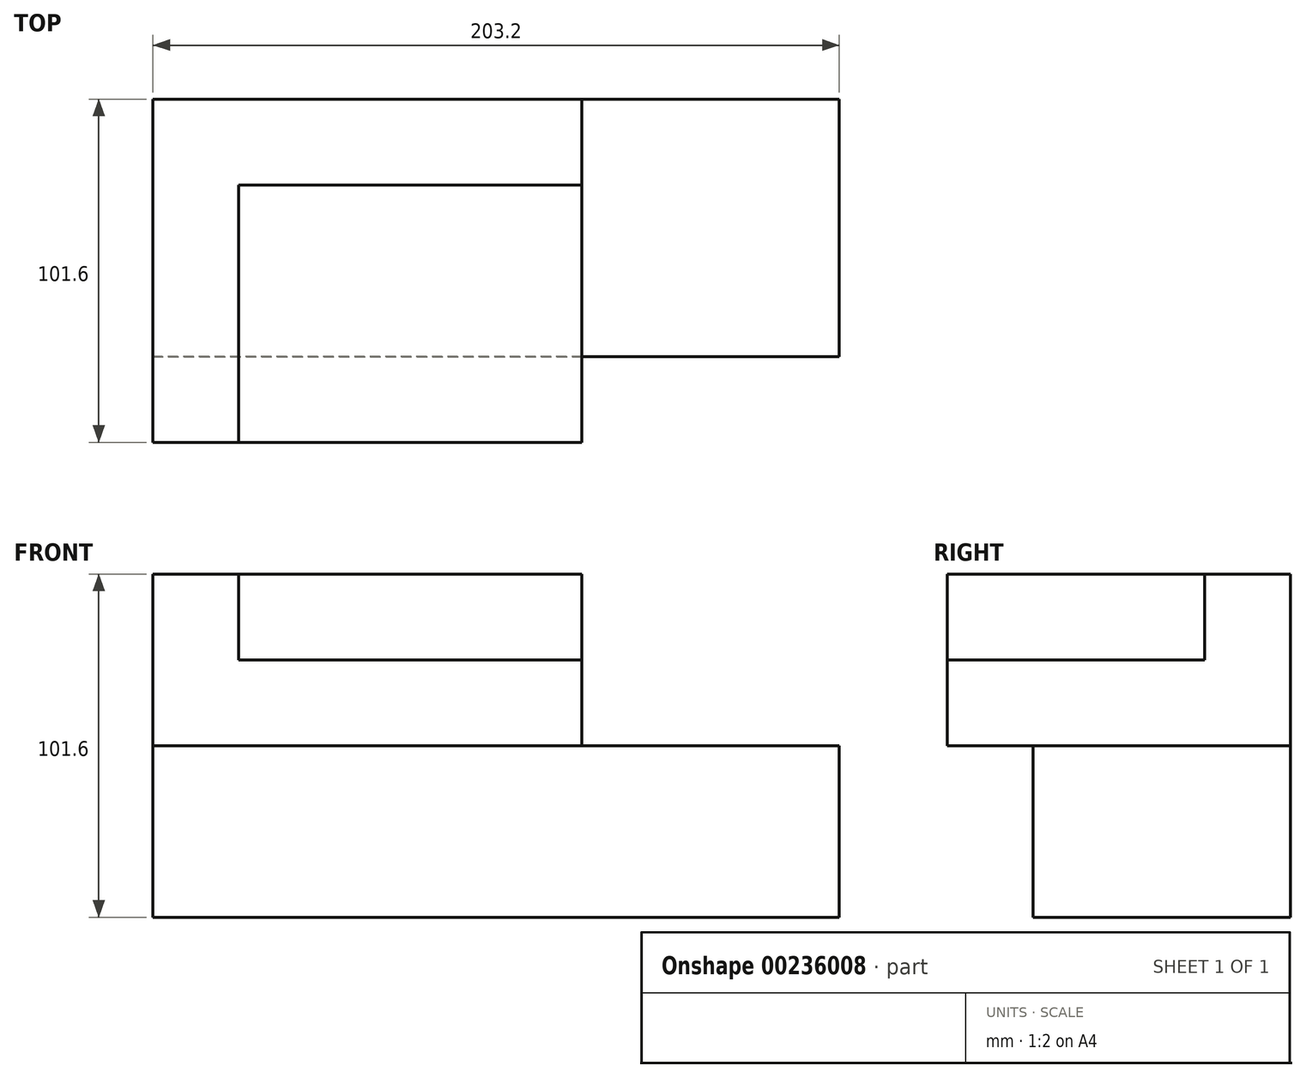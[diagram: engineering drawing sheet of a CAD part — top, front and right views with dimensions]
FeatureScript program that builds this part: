
annotation { "Feature Type Name" : "Feature", "Feature Type Description" : "" }
export const myFeature = defineFeature(function(context is Context, id is Id, definition is map)
    precondition{}
    {
        {
            var Q0;
            Q0=qCreatedBy(makeId("Top.planeOp"),FACE);
            var sketch = newSketch(context, id + "F0", { "sketchPlane" : qUnion([Q0])});
            skLineSegment(sketch, "E0.bottom", {"start": v(-172.4, -39.52) * mm, "end": v(30.8, -39.52) * mm});
            skLineSegment(sketch, "E0.top", {"start": v(-172.4, 36.68) * mm, "end": v(30.8, 36.68) * mm});
            skLineSegment(sketch, "E0.left", {"start": v(-172.4, -39.52) * mm, "end": v(-172.4, 36.68) * mm});
            skLineSegment(sketch, "E0.right", {"start": v(30.8, -39.52) * mm, "end": v(30.8, 36.68) * mm});
            skSolve(sketch);
        }
        {
            var Q0;
            Q0=makeQuery(id+"F0.imprint","IMPRINT",FACE,{"disambiguationData":[TD([[makeQuery(id+"F0.imprint","IMPRINT",EDGE,{"derivedFrom":sQuery(id+"F0.wireOp",EDGE,"E0.bottom")}),1.0]])]});
            extrude(context, id + "F1", {"entities" : qUnion([Q0]), "depth" : 50.8 * mm});
        }
        {
            var Q0;
            Q0=makeQuery(id+"F1.opExtrude","CAP_FACE",FACE,{"disambiguationData":[OSD([sQuery(id+"F0.wireOp",EDGE,"E0.bottom"),sQuery(id+"F0.wireOp",EDGE,"E0.top"),sQuery(id+"F0.wireOp",EDGE,"E0.left"),sQuery(id+"F0.wireOp",EDGE,"E0.right")])],"isStart":false});
            var sketch = newSketch(context, id + "F2", { "sketchPlane" : qUnion([Q0])});
            skLineSegment(sketch, "E1.bottom", {"start": v(-172.4, 36.68) * mm, "end": v(-45.4, 36.68) * mm});
            skLineSegment(sketch, "E1.top", {"start": v(-172.4, -64.92) * mm, "end": v(-45.4, -64.92) * mm});
            skLineSegment(sketch, "E1.left", {"start": v(-172.4, 36.68) * mm, "end": v(-172.4, -64.92) * mm});
            skLineSegment(sketch, "E1.right", {"start": v(-45.4, 36.68) * mm, "end": v(-45.4, -64.92) * mm});
            skSolve(sketch);
        }
        {
            var Q0;
            {var subQ0=sQuery(id+"F2.wireOp",EDGE,"E1.bottom");Q0=makeQuery(id+"F2.imprint","IMPRINT",FACE,{"disambiguationData":[TD([[makeQuery(id+"F2.imprint","IMPRINT",EDGE,{"derivedFrom":subQ0}),-1.0]])]});}
            extrude(context, id + "F3", {"entities" : qUnion([Q0]), "operationType" : NewBodyOperationType.ADD, "depth" : 25.4 * mm});
        }
        {
            var Q0;
            {var subQ0=sQuery(id+"F0.wireOp",EDGE,"E0.bottom");Q0=makeQuery(id+"F3.boolean.opBoolean","MERGE",FACE,{"derivedFrom":[makeQuery(id+"F1.opExtrude","SWEPT_FACE",FACE,{"disambiguationData":[OSD([subQ0])]}),makeQuery(id+"F3.opExtrude","SWEPT_FACE",FACE,{"disambiguationData":[OSD([subQ0])]})]});}
            var sketch = newSketch(context, id + "F4", { "sketchPlane" : qUnion([Q0])});
            skLineSegment(sketch, "E2", {"start": v(-45.4, 50.8) * mm, "end": v(-172.4, 50.8) * mm});
            skSolve(sketch);
        }
        {
            var Q0;
            {var subQ0=sQuery(id+"F4.wireOp",EDGE,"E2");Q0=makeQuery(id+"F4.imprint","IMPRINT",FACE,{"disambiguationData":[TD([[makeQuery(id+"F4.imprint","IMPRINT",EDGE,{"derivedFrom":subQ0}),-1.0]])]});}
            extrude(context, id + "F5", {"entities" : qUnion([Q0]), "operationType" : NewBodyOperationType.ADD, "depth" : 25.4 * mm});
        }
        {
            var Q0;
            {var subQ0=sQuery(id+"F0.wireOp",EDGE,"E0.bottom");Q0=makeQuery(id+"F5.boolean.opBoolean","MERGE",FACE,{"derivedFrom":[makeQuery(id+"F3.opExtrude","CAP_FACE",FACE,{"disambiguationData":[OSD([subQ0,sQuery(id+"F2.wireOp",EDGE,"E1.bottom"),sQuery(id+"F2.wireOp",EDGE,"E1.left"),sQuery(id+"F2.wireOp",EDGE,"E1.right")])],"isStart":false}),makeQuery(id+"F5.opExtrude","SWEPT_FACE",FACE,{"disambiguationData":[OSD([subQ0])]})]});}
            var sketch = newSketch(context, id + "F6", { "sketchPlane" : qUnion([Q0])});
            skLineSegment(sketch, "E3", {"start": v(-172.4, -64.92) * mm, "end": v(-147, -64.92) * mm});
            skLineSegment(sketch, "E4", {"start": v(-147, -64.92) * mm, "end": v(-147, 36.68) * mm});
            skSolve(sketch);
        }
        {
            var Q0;
            Q0=makeQuery(id+"F6.imprint","IMPRINT",FACE,{"disambiguationData":[TD([[makeQuery(id+"F6.imprint","IMPRINT",EDGE,{"derivedFrom":sQuery(id+"F6.wireOp",EDGE,"E3")}),1.0]])]});
            extrude(context, id + "F7", {"entities" : qUnion([Q0]), "operationType" : NewBodyOperationType.ADD, "depth" : 25.4 * mm});
        }
        {
            var Q0;
            Q0=makeQuery(id+"F7.opExtrude","SWEPT_FACE",FACE,{"disambiguationData":[OSD([sQuery(id+"F6.wireOp",EDGE,"E4")])]});
            var sketch = newSketch(context, id + "F8", { "sketchPlane" : qUnion([Q0])});
            skLineSegment(sketch, "E5", {"start": v(36.68, 101.6) * mm, "end": v(11.28, 101.6) * mm});
            skLineSegment(sketch, "E6", {"start": v(11.28, 101.6) * mm, "end": v(11.28, 76.2) * mm});
            skSolve(sketch);
        }
        {
            var Q0;
            Q0=makeQuery(id+"F8.imprint","IMPRINT",FACE,{"disambiguationData":[TD([[makeQuery(id+"F8.imprint","IMPRINT",EDGE,{"derivedFrom":sQuery(id+"F8.wireOp",EDGE,"E5")}),-1.0]])]});
            extrude(context, id + "F9", {"entities" : qUnion([Q0]), "operationType" : NewBodyOperationType.ADD, "depth" : 101.6 * mm});
        }
    });
